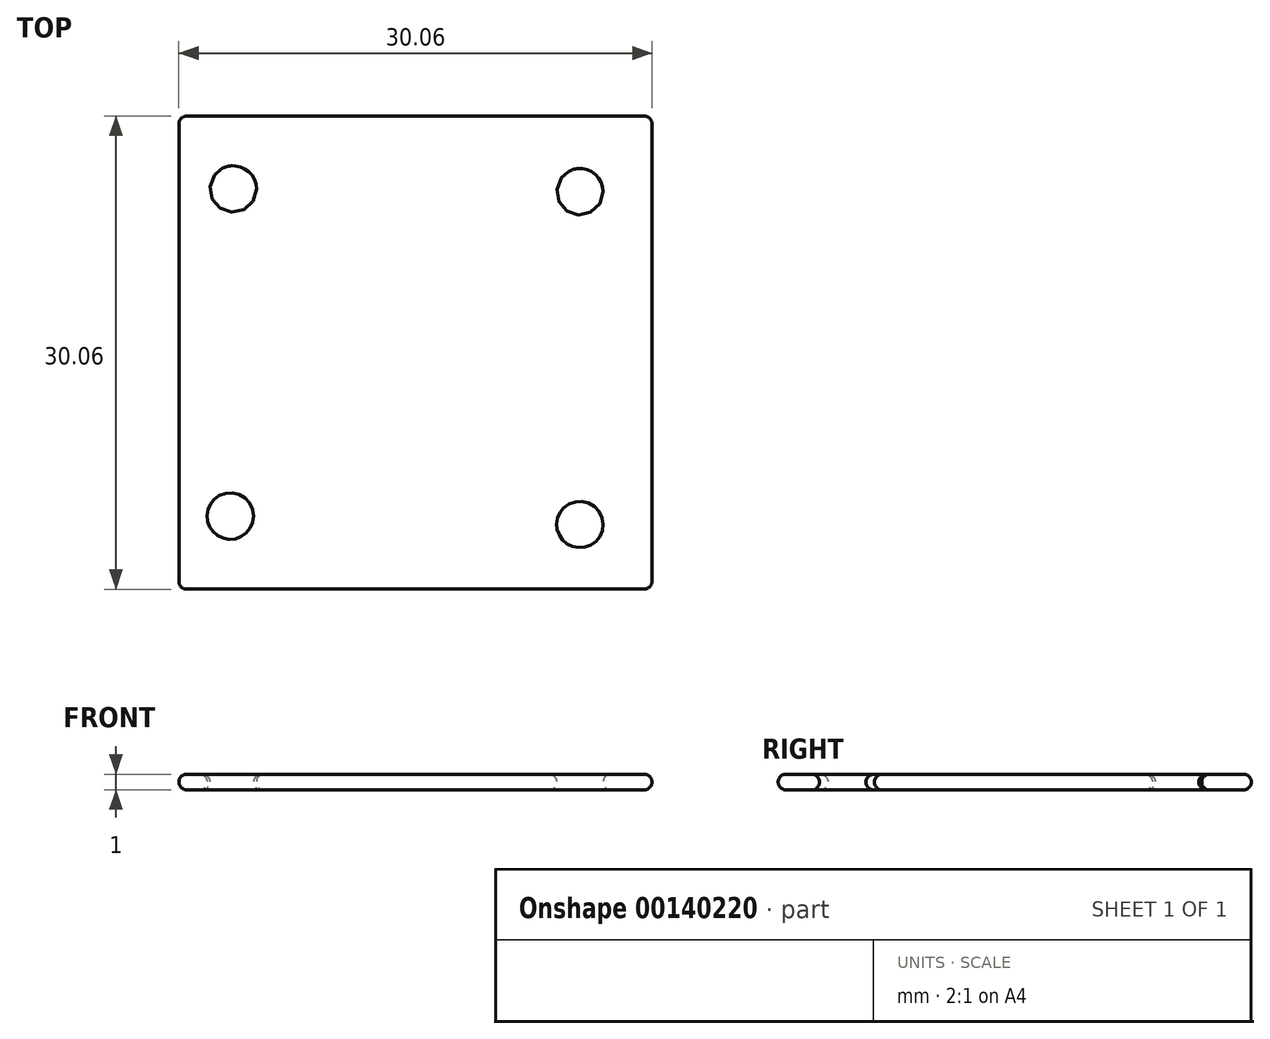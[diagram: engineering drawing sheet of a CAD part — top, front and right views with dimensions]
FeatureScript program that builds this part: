
annotation { "Feature Type Name" : "Feature", "Feature Type Description" : "" }
export const myFeature = defineFeature(function(context is Context, id is Id, definition is map)
    precondition{}
    {
        {
            var Q0;
            Q0=qCreatedBy(makeId("Top.planeOp"),FACE);
            var sketch = newSketch(context, id + "F0", { "sketchPlane" : qUnion([Q0])});
            skLineSegment(sketch, "E0.bottom", {"start": v(15, 15) * mm, "end": v(-15, 15) * mm});
            skLineSegment(sketch, "E0.top", {"start": v(15, -15) * mm, "end": v(-15, -15) * mm});
            skLineSegment(sketch, "E0.left", {"start": v(15, 15) * mm, "end": v(15, -15) * mm});
            skLineSegment(sketch, "E0.right", {"start": v(-15, 15) * mm, "end": v(-15, -15) * mm});
            skPoint(sketch, "E0.middle", {"position": v(0, 0) * mm});
            skCircle(sketch, "E1", {"center": v(10.44, 10.22) * mm, "radius": 1.5 * mm});
            skCircle(sketch, "E2", {"center": v(-11.58, 10.4) * mm, "radius": 1.5 * mm});
            skCircle(sketch, "E3", {"center": v(-11.76, -10.39) * mm, "radius": 1.5 * mm});
            skCircle(sketch, "E4", {"center": v(10.44, -10.92) * mm, "radius": 1.5 * mm});
            skSolve(sketch);
        }
        {
            var Q0;
            Q0=makeQuery(id+"F0.imprint","IMPRINT",FACE,{"disambiguationData":[TD([[makeQuery(id+"F0.imprint","IMPRINT",EDGE,{"derivedFrom":sQuery(id+"F0.wireOp",EDGE,"E0.bottom")}),1.0]])]});
            extrude(context, id + "F1", {"entities" : qUnion([Q0]), "depth" : 1 * mm, "hasDraft" : true, "draftAngle" : 3 * degree});
        }
        {
            var Q0;
            Q0=makeQuery(id+"F1.opExtrude","CAP_EDGE",EDGE,{"disambiguationData":[OSD([sQuery(id+"F0.wireOp",EDGE,"E0.top")])],"isStart":false});
            var Q1;
            Q1=makeQuery(id+"F1.opExtrude","CAP_EDGE",EDGE,{"disambiguationData":[OSD([sQuery(id+"F0.wireOp",EDGE,"E0.top")])],"isStart":true});
            var Q2;
            Q2=makeQuery(id+"F1.opExtrude","CAP_EDGE",EDGE,{"disambiguationData":[OSD([sQuery(id+"F0.wireOp",EDGE,"E0.right")])],"isStart":true});
            var Q3;
            Q3=makeQuery(id+"F1.opExtrude","CAP_EDGE",EDGE,{"disambiguationData":[OSD([sQuery(id+"F0.wireOp",EDGE,"E0.right")])],"isStart":false});
            var Q4;
            Q4=makeQuery(id+"F1.opExtrude","CAP_EDGE",EDGE,{"disambiguationData":[OSD([sQuery(id+"F0.wireOp",EDGE,"E0.left")])],"isStart":false});
            var Q5;
            Q5=makeQuery(id+"F1.opExtrude","CAP_EDGE",EDGE,{"disambiguationData":[OSD([sQuery(id+"F0.wireOp",EDGE,"E0.bottom")])],"isStart":false});
            var Q6;
            Q6=makeQuery(id+"F1.opExtrude","CAP_EDGE",EDGE,{"disambiguationData":[OSD([sQuery(id+"F0.wireOp",EDGE,"E0.bottom")])],"isStart":true});
            var Q7;
            Q7=makeQuery(id+"F1.opExtrude","CAP_EDGE",EDGE,{"disambiguationData":[OSD([sQuery(id+"F0.wireOp",EDGE,"E0.left")])],"isStart":true});
            var Q8;
            Q8=makeQuery(id+"F1.opExtrude","SWEPT_EDGE",EDGE,{"disambiguationData":[OSD([sQuery(id+"F0.wireOp",EDGE,"E0.top"),sQuery(id+"F0.wireOp",EDGE,"E0.right")])]});
            var Q9;
            Q9=makeQuery(id+"F1.opExtrude","SWEPT_EDGE",EDGE,{"disambiguationData":[OSD([sQuery(id+"F0.wireOp",EDGE,"E0.top"),sQuery(id+"F0.wireOp",EDGE,"E0.left")])]});
            var Q10;
            Q10=makeQuery(id+"F1.opExtrude","SWEPT_EDGE",EDGE,{"disambiguationData":[OSD([sQuery(id+"F0.wireOp",EDGE,"E0.bottom"),sQuery(id+"F0.wireOp",EDGE,"E0.right")])]});
            var Q11;
            Q11=makeQuery(id+"F1.opExtrude","SWEPT_EDGE",EDGE,{"disambiguationData":[OSD([sQuery(id+"F0.wireOp",EDGE,"E0.bottom"),sQuery(id+"F0.wireOp",EDGE,"E0.left")])]});
            fillet(context, id + "F2", {"entities" : qUnion([Q0, Q1, Q2, Q3, Q4, Q5, Q6, Q7, Q8, Q9, Q10, Q11]), "radius" : 0.5 * mm, "tangentPropagation" : true, "allowEdgeOverflow" : false});
        }
        {
            var Q0;
            Q0=makeQuery(id+"F1.opExtrude","CAP_EDGE",EDGE,{"disambiguationData":[OSD([sQuery(id+"F0.wireOp",EDGE,"E4")])],"isStart":false});
            var Q1;
            Q1=makeQuery(id+"F1.opExtrude","CAP_EDGE",EDGE,{"disambiguationData":[OSD([sQuery(id+"F0.wireOp",EDGE,"E3")])],"isStart":false});
            var Q2;
            Q2=makeQuery(id+"F1.opExtrude","CAP_EDGE",EDGE,{"disambiguationData":[OSD([sQuery(id+"F0.wireOp",EDGE,"E2")])],"isStart":false});
            var Q3;
            Q3=makeQuery(id+"F1.opExtrude","CAP_EDGE",EDGE,{"disambiguationData":[OSD([sQuery(id+"F0.wireOp",EDGE,"E1")])],"isStart":false});
            var Q4;
            Q4=makeQuery(id+"F1.opExtrude","CAP_EDGE",EDGE,{"disambiguationData":[OSD([sQuery(id+"F0.wireOp",EDGE,"E4")])],"isStart":true});
            var Q5;
            Q5=makeQuery(id+"F1.opExtrude","CAP_EDGE",EDGE,{"disambiguationData":[OSD([sQuery(id+"F0.wireOp",EDGE,"E3")])],"isStart":true});
            var Q6;
            Q6=makeQuery(id+"F1.opExtrude","CAP_EDGE",EDGE,{"disambiguationData":[OSD([sQuery(id+"F0.wireOp",EDGE,"E2")])],"isStart":true});
            var Q7;
            Q7=makeQuery(id+"F1.opExtrude","CAP_EDGE",EDGE,{"disambiguationData":[OSD([sQuery(id+"F0.wireOp",EDGE,"E1")])],"isStart":true});
            fillet(context, id + "F3", {"entities" : qUnion([Q0, Q1, Q2, Q3, Q4, Q5, Q6, Q7]), "radius" : 0.5 * mm, "tangentPropagation" : true, "allowEdgeOverflow" : false});
        }
    });
